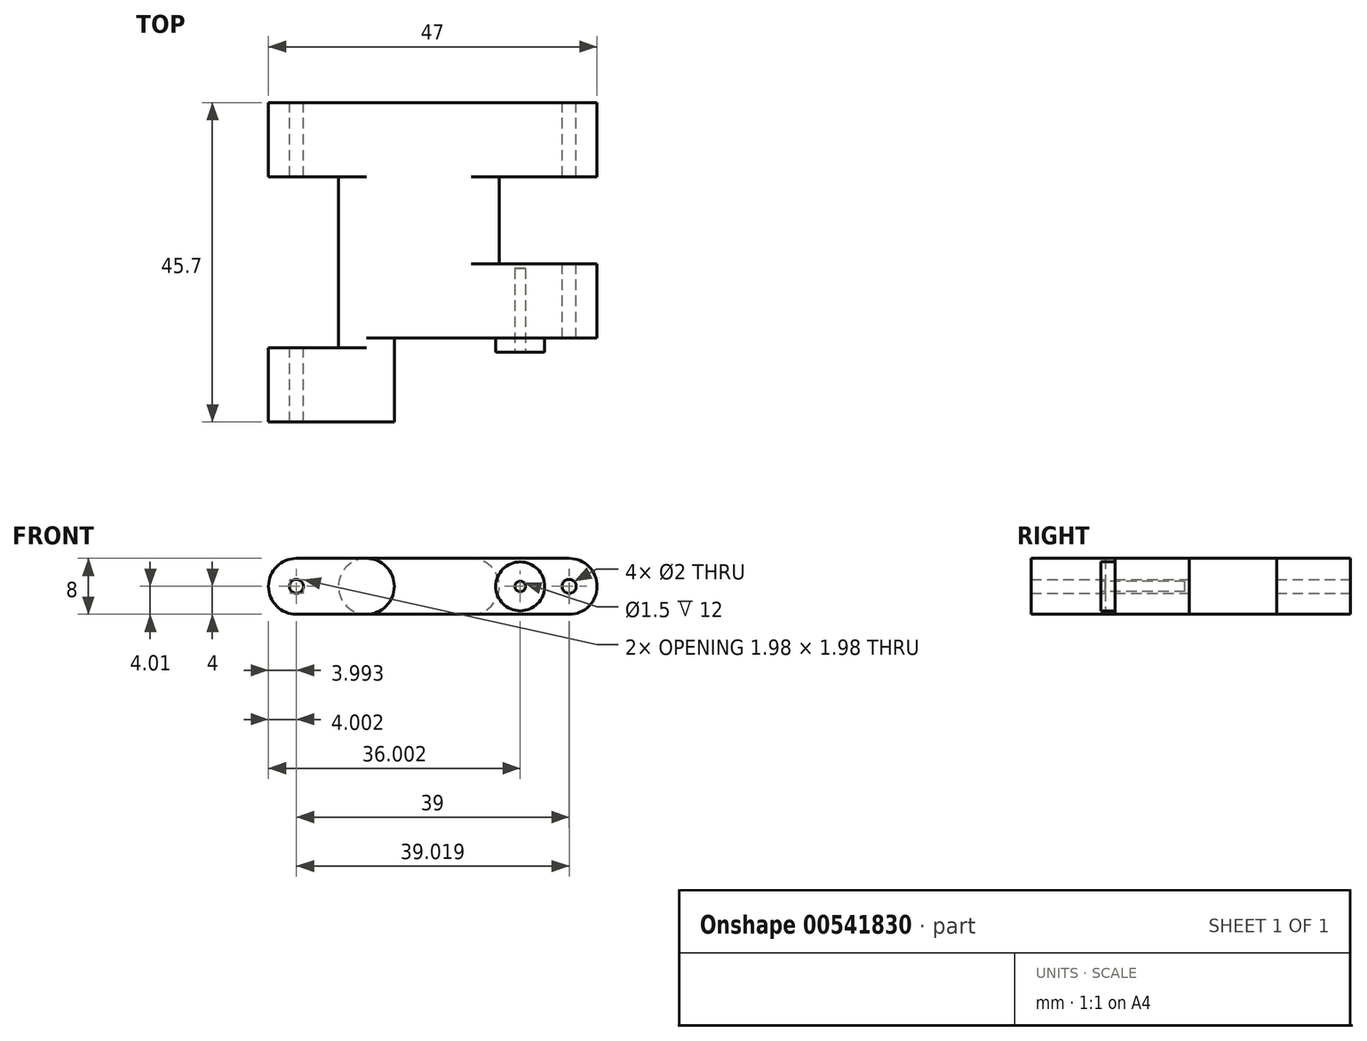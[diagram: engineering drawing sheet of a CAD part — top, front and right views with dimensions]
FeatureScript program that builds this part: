
annotation { "Feature Type Name" : "Feature", "Feature Type Description" : "" }
export const myFeature = defineFeature(function(context is Context, id is Id, definition is map)
    precondition{}
    {
        {
            var Q0;
            Q0=qCreatedBy(makeId("Top.planeOp"),FACE);
            var sketch = newSketch(context, id + "F0", { "sketchPlane" : qUnion([Q0])});
            skLineSegment(sketch, "E0", {"start": v(-19.9, -12.52) * mm, "end": v(-1.9, -12.52) * mm});
            skLineSegment(sketch, "E1", {"start": v(-1.9, -12.52) * mm, "end": v(-1.9, -0.52) * mm});
            skLineSegment(sketch, "E2", {"start": v(-1.9, -0.52) * mm, "end": v(27.1, -0.52) * mm});
            skLineSegment(sketch, "E3", {"start": v(27.1, -0.52) * mm, "end": v(27.1, 10.08) * mm});
            skLineSegment(sketch, "E4", {"start": v(27.1, 10.08) * mm, "end": v(13.1, 10.08) * mm});
            skLineSegment(sketch, "E5", {"start": v(13.1, 10.08) * mm, "end": v(13.1, 22.58) * mm});
            skLineSegment(sketch, "E6", {"start": v(13.1, 22.58) * mm, "end": v(27.1, 22.58) * mm});
            skLineSegment(sketch, "E7", {"start": v(27.1, 22.58) * mm, "end": v(27.1, 33.18) * mm});
            skLineSegment(sketch, "E8", {"start": v(27.1, 33.18) * mm, "end": v(-19.9, 33.18) * mm});
            skLineSegment(sketch, "E9", {"start": v(-19.9, 33.18) * mm, "end": v(-19.9, 22.58) * mm});
            skLineSegment(sketch, "E10", {"start": v(-19.9, 22.58) * mm, "end": v(-9.9, 22.58) * mm});
            skLineSegment(sketch, "E11", {"start": v(-9.9, 22.58) * mm, "end": v(-9.9, -1.92) * mm});
            skLineSegment(sketch, "E12", {"start": v(-9.9, -1.92) * mm, "end": v(-19.9, -1.92) * mm});
            skLineSegment(sketch, "E13", {"start": v(-19.9, -1.92) * mm, "end": v(-19.9, -12.52) * mm});
            skSolve(sketch);
        }
        {
            var Q0;
            Q0=makeQuery(id+"F0.imprint","IMPRINT",FACE,{"disambiguationData":[TD([[makeQuery(id+"F0.imprint","IMPRINT",EDGE,{"derivedFrom":sQuery(id+"F0.wireOp",EDGE,"E0")}),1.0]])]});
            extrude(context, id + "F1", {"entities" : qUnion([Q0]), "depth" : 8 * mm});
        }
        {
            var Q0;
            Q0=makeQuery(id+"F1.opExtrude","CAP_EDGE",EDGE,{"disambiguationData":[OSD([sQuery(id+"F0.wireOp",EDGE,"E13")])],"isStart":false});
            var Q1;
            Q1=makeQuery(id+"F1.opExtrude","CAP_EDGE",EDGE,{"disambiguationData":[OSD([sQuery(id+"F0.wireOp",EDGE,"E13")])],"isStart":true});
            var Q2;
            Q2=makeQuery(id+"F1.opExtrude","CAP_EDGE",EDGE,{"disambiguationData":[OSD([sQuery(id+"F0.wireOp",EDGE,"E1")])],"isStart":false});
            var Q3;
            Q3=makeQuery(id+"F1.opExtrude","CAP_EDGE",EDGE,{"disambiguationData":[OSD([sQuery(id+"F0.wireOp",EDGE,"E1")])],"isStart":true});
            var Q4;
            Q4=makeQuery(id+"F1.opExtrude","CAP_EDGE",EDGE,{"disambiguationData":[OSD([sQuery(id+"F0.wireOp",EDGE,"E3")])],"isStart":false});
            var Q5;
            Q5=makeQuery(id+"F1.opExtrude","CAP_EDGE",EDGE,{"disambiguationData":[OSD([sQuery(id+"F0.wireOp",EDGE,"E3")])],"isStart":true});
            var Q6;
            Q6=makeQuery(id+"F1.opExtrude","CAP_EDGE",EDGE,{"disambiguationData":[OSD([sQuery(id+"F0.wireOp",EDGE,"E7")])],"isStart":false});
            var Q7;
            Q7=makeQuery(id+"F1.opExtrude","CAP_EDGE",EDGE,{"disambiguationData":[OSD([sQuery(id+"F0.wireOp",EDGE,"E7")])],"isStart":true});
            var Q8;
            Q8=makeQuery(id+"F1.opExtrude","CAP_EDGE",EDGE,{"disambiguationData":[OSD([sQuery(id+"F0.wireOp",EDGE,"E9")])],"isStart":false});
            var Q9;
            Q9=makeQuery(id+"F1.opExtrude","CAP_EDGE",EDGE,{"disambiguationData":[OSD([sQuery(id+"F0.wireOp",EDGE,"E9")])],"isStart":true});
            fillet(context, id + "F2", {"entities" : qUnion([Q0, Q1, Q2, Q3, Q4, Q5, Q6, Q7, Q8, Q9]), "radius" : 4 * mm, "tangentPropagation" : true, "allowEdgeOverflow" : false});
        }
        {
            var Q0;
            Q0=makeQuery(id+"F1.opExtrude","SWEPT_FACE",FACE,{"disambiguationData":[OSD([sQuery(id+"F0.wireOp",EDGE,"E8")])]});
            var sketch = newSketch(context, id + "F3", { "sketchPlane" : qUnion([Q0])});
            skCircle(sketch, "E14", {"center": v(-23.1, 4) * mm, "radius": 1 * mm});
            skCircle(sketch, "E15", {"center": v(15.9, 4) * mm, "radius": 1 * mm});
            skSolve(sketch);
        }
        {
            var Q0;
            Q0=qSketchRegion(id+"F3",true);
            extrude(context, id + "F4", {"entities" : qUnion([Q0]), "operationType" : NewBodyOperationType.REMOVE, "oppositeDirection" : true, "depth" : 60 * mm});
        }
        {
            var Q0;
            Q0=makeQuery(id+"F1.opExtrude","SWEPT_FACE",FACE,{"disambiguationData":[OSD([sQuery(id+"F0.wireOp",EDGE,"E2")])]});
            var sketch = newSketch(context, id + "F5", { "sketchPlane" : qUnion([Q0])});
            skCircle(sketch, "E16", {"center": v(16.1, 4) * mm, "radius": 3.5 * mm});
            skPoint(sketch, "E16.centerSnap0", {"position": v(27.1, 4) * mm});
            skSolve(sketch);
        }
        {
            var Q0;
            Q0=makeQuery(id+"F1.opExtrude","CAP_EDGE",EDGE,{"disambiguationData":[OSD([sQuery(id+"F0.wireOp",EDGE,"E11")])],"isStart":false});
            var Q1;
            Q1=makeQuery(id+"F1.opExtrude","CAP_EDGE",EDGE,{"disambiguationData":[OSD([sQuery(id+"F0.wireOp",EDGE,"E11")])],"isStart":true});
            var Q2;
            Q2=makeQuery(id+"F1.opExtrude","CAP_EDGE",EDGE,{"disambiguationData":[OSD([sQuery(id+"F0.wireOp",EDGE,"E5")])],"isStart":false});
            var Q3;
            Q3=makeQuery(id+"F1.opExtrude","CAP_EDGE",EDGE,{"disambiguationData":[OSD([sQuery(id+"F0.wireOp",EDGE,"E5")])],"isStart":true});
            fillet(context, id + "F6", {"entities" : qUnion([Q0, Q1, Q2, Q3]), "radius" : 4 * mm, "tangentPropagation" : true, "allowEdgeOverflow" : false});
        }
        {
            var Q0;
            Q0=qSketchRegion(id+"F5",true);
            extrude(context, id + "F7", {"entities" : qUnion([Q0]), "operationType" : NewBodyOperationType.ADD, "depth" : 2 * mm});
        }
        {
            var Q0;
            Q0=makeQuery(id+"F7.opExtrude","CAP_FACE",FACE,{"disambiguationData":[OSD([sQuery(id+"F5.wireOp",EDGE,"E16")])],"isStart":false});
            var sketch = newSketch(context, id + "F8", { "sketchPlane" : qUnion([Q0])});
            skCircle(sketch, "E17", {"center": v(16.1, 4) * mm, "radius": 0.75 * mm});
            skSolve(sketch);
        }
        {
            var Q0;
            Q0=makeQuery(id+"F8.imprint","IMPRINT",FACE,{"disambiguationData":[TD([[makeQuery(id+"F8.imprint","IMPRINT",EDGE,{"derivedFrom":sQuery(id+"F8.wireOp",EDGE,"E17")}),1.0]])]});
            extrude(context, id + "F9", {"entities" : qUnion([Q0]), "operationType" : NewBodyOperationType.REMOVE, "oppositeDirection" : true, "depth" : 12 * mm});
        }
    });
